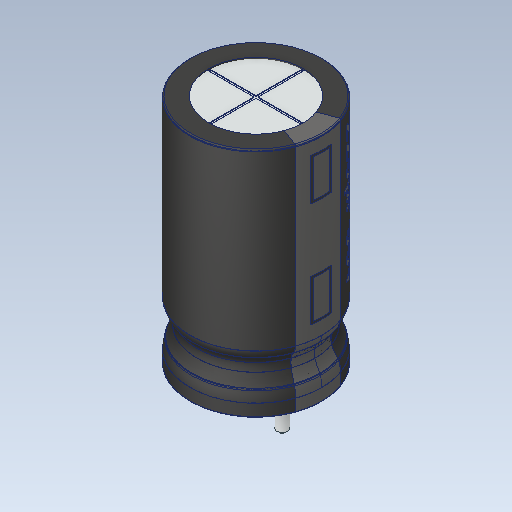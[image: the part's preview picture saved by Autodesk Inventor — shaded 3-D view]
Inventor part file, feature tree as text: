
AUTODESK INVENTOR PART (.ipt)
format: ipt  version: 2020 (Build 240168000, 168)  size: 705,536 bytes
history: native  units: in
note: dims shown in document units (in); Inventor stores cm internally (conversion verified against a paired STEP export)
features: other x4, fillet x2, extrude x1, chamfer x1, sketch x1, projected_geometry x1
ambient origin geometry x8: Origin, YZ Plane, XZ Plane, XY Plane, X Axis, Y Axis, Z Axis, Center Point
bodies: Solid1 (feature_tree), Solid2 (feature_tree), Solid3 (feature_tree), Solid4 (feature_tree), Solid5 (feature_tree), Solid6 (feature_tree)
feature tree (10):
  extrude  "Extrusion1"  TaperAngle=0.0deg  [1 undecoded]
  chamfer  "Chamfer1"  Distance=0.005in Angle=45.0deg
  sketch  "Sketch1"  dims[d0=0.085in d1=0.0in d2=0.0in d3=0.005in d4=0.125in d5=45.0deg]
  projected_geometry  "Projected Loop1"
  other  "Cut-Extrude4"
  other  "Cut-Extrude5"
  other  "Boss-Extrude7[2]"
  other  "Boss-Extrude8"
  fillet  "Fillet5"  [1 undecoded]
  fillet  "Fillet6"  [1 undecoded]
note: 3 required parameter values undecoded (feature->parameter linkage not recoverable at this tier; creation-order binding heuristic only, values carry confidence <= 0.55)
